# Revit family: Wall-Panel_Terra-Cotta-Rainscreen
name_source: partatom
category: Curtain Panels
units: mm (PartAtom-declared; Revit-internal decimal feet)

## family parameters
Always vertical = Yes
Classification Number = 23.35.06.21
Cut with Voids When Loaded = No
Shared = No

## types (1)
- ByType
    Assembly Code = B20
    Clip Offset = 0' - 1"
    Clip Thickness = 0' - 0 1/4"
    Clips-Panel = 4
    Construction Details = http://www.arcat.com
    Description = Metal Rainscreen Panel
    Expected Lifespan (Years) = 30
    Green Building-LEED = http://www.arcat.com
    Groove Depth = 0' - 1 3/4"
    Hardware Material = ARCAT - Metal - Aluminum - B209_5005_H-14 - Anodized
    Keynote = 07410
    Maintenance Schedule (Months) = 24
    Manufacturer = "Generic"
    Manufacturer Fax = (203) 929-2444
    Manufacturer Website = http://www.arcat.com
    Model = "Generic"
    Nose = 0' - 0 1/4"
    Offset = 0' - 0 3/8"
    Panel Gap = 0' - 0 3/4"
    Panel Thickness = 0' - 1"
    Product Data = http://www.arcat.com
    Product Properties = http://www.arcat.com
    Recyclable = No
    Specification = http://www.arcat.com
    Tongue Length = 0' - 1 1/2"
    Warranty Duration (Years) = 10

## geometry (parser evidence)
native form markers: Sweep x2
no freeform markers — native parametric forms only
